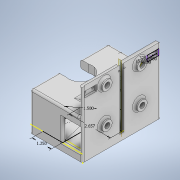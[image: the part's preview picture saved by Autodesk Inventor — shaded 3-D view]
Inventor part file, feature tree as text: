
AUTODESK INVENTOR PART (.ipt)
format: ipt  version: 2020 (Build 240168000, 168)  size: 501,248 bytes
history: native  units: in
note: dims shown in document units (in); Inventor stores cm internally (conversion verified against a paired STEP export)
features: sketch x18, extrude x14, hole x4, plane x1, mirror x1, fillet x1
ambient origin geometry x8: Origin, YZ Plane, XZ Plane, XY Plane, X Axis, Y Axis, Z Axis, Center Point
bodies: Solid1 (feature_tree)
feature tree (39):
  extrude  "Extrusion1"  Depth=5.0299in
  extrude  "Extrusion2"  Depth=0.375in
  extrude  "Extrusion3"  Depth=2.8543in
  sketch  "Sketch5"  dims[d24=5.315in d25=4.5472in]
  extrude  "Extrusion4"  Depth=4.5472in
  extrude  "Extrusion5"  Depth=0.25in
  extrude  "Extrusion6"  Depth=2.6575in
  hole  "Hole2"  [1 undecoded]
  extrude  "Extrusion7"  Depth=0.5in
  extrude  "Extrusion8"  Depth=1.5in
  extrude  "Extrusion9"  Depth=0.5in
  extrude  "Extrusion10"  Depth=0.5in
  hole  "Hole3"  [1 undecoded]
  extrude  "Extrusion11"  Depth=1.5in TaperAngle=0.0deg
  extrude  "Extrusion12"  Depth=1.125in
  hole  "Hole4"  [1 undecoded]
  sketch  "Sketch17"  dims[d63=2.25in d64=90.0deg]
  extrude  "Extrusion13"  TaperAngle=90.0deg  [1 undecoded]
  hole  "Hole5"  [1 undecoded]
  plane  "Work Plane1"
  mirror  "Mirror1"
  extrude  "Extrusion14"  TaperAngle=0.0deg  [1 undecoded]
  fillet  "Fillet1"  Radius=0.625in
  sketch  "Sketch18"  dims[d65=2.25in d66=90.0deg]
  sketch  "Sketch1"  dims[d0=3.3654in d1=5.0299in]
  sketch  "Sketch3"  dims[d3=45.0deg d4=0.375in]
  sketch  "Sketch4"  dims[d5=0.5in d6=0.0in d23=2.8543in]
  sketch  "Sketch6"  dims[d26=0.1in d27=0.0in d28=0.25in]
  sketch  "Sketch7"  dims[d29=0.1in d30=0.0in d31=2.6575in]
  sketch  "Sketch8"  dims[d32=1.5in d33=1.25in]
  sketch  "Sketch9"  dims[d34=1.9685in d35=0.0in d36=0.5in]
  sketch  "Sketch10"  dims[d37=5.03in d38=0.0in d39=1.5in]
  sketch  "Sketch11"  dims[d40=1.0in d41=0.0in d42=0.5in]
  sketch  "Sketch12"  dims[d43=0.0in d44=0.5in]
  sketch  "Sketch13"  dims[d45=0.201in d46=0.75in d47=0.385in d48=0.25in d49=0.5635in d50=1.378in d51=0.0in d52=1.9685in d53=0.0in]
  sketch  "Sketch14"  dims[d54=1.9685in d55=0.0in d56=1.5in d57=0.0in]
  sketch  "Sketch15"  dims[d58=3.75in d59=0.0in d60=1.125in]
  sketch  "Sketch16"  dims[d61=1.49in d62=2.25in]
  sketch  "Sketch19"  dims[d67=0.332in d68=0.375in d69=0.119in d70=0.25in d71=0.5635in d72=0.375in d73=0.0in d74=0.0in d75=0.0in d76=0.625in d77=0.625in d78=0.625in d79=0.625in d80=0.2in d81=0.0in d82=0.21in d83=1.125in d84=0.185in d85=0.37in d86=0.09in d87=0.375in d88=0.119in d89=0.25in d90=0.5635in d91=0.375in d92=0.0in d93=0.375in d94=0.0in d95=0.25in d96=0.5in d97=0.375in d98=0.125in d99=0.0in d100=0.129in d101=0.198in d102=0.225in d103=0.188in d104=0.5635in d105=0.375in d106=0.0in d107=0.125in d108=0.125in d109=1.0in d110=1.0in d111=0.5in d112=1.25in d113=0.0in]
note: 6 required parameter values undecoded (feature->parameter linkage not recoverable at this tier; creation-order binding heuristic only, values carry confidence <= 0.55)
